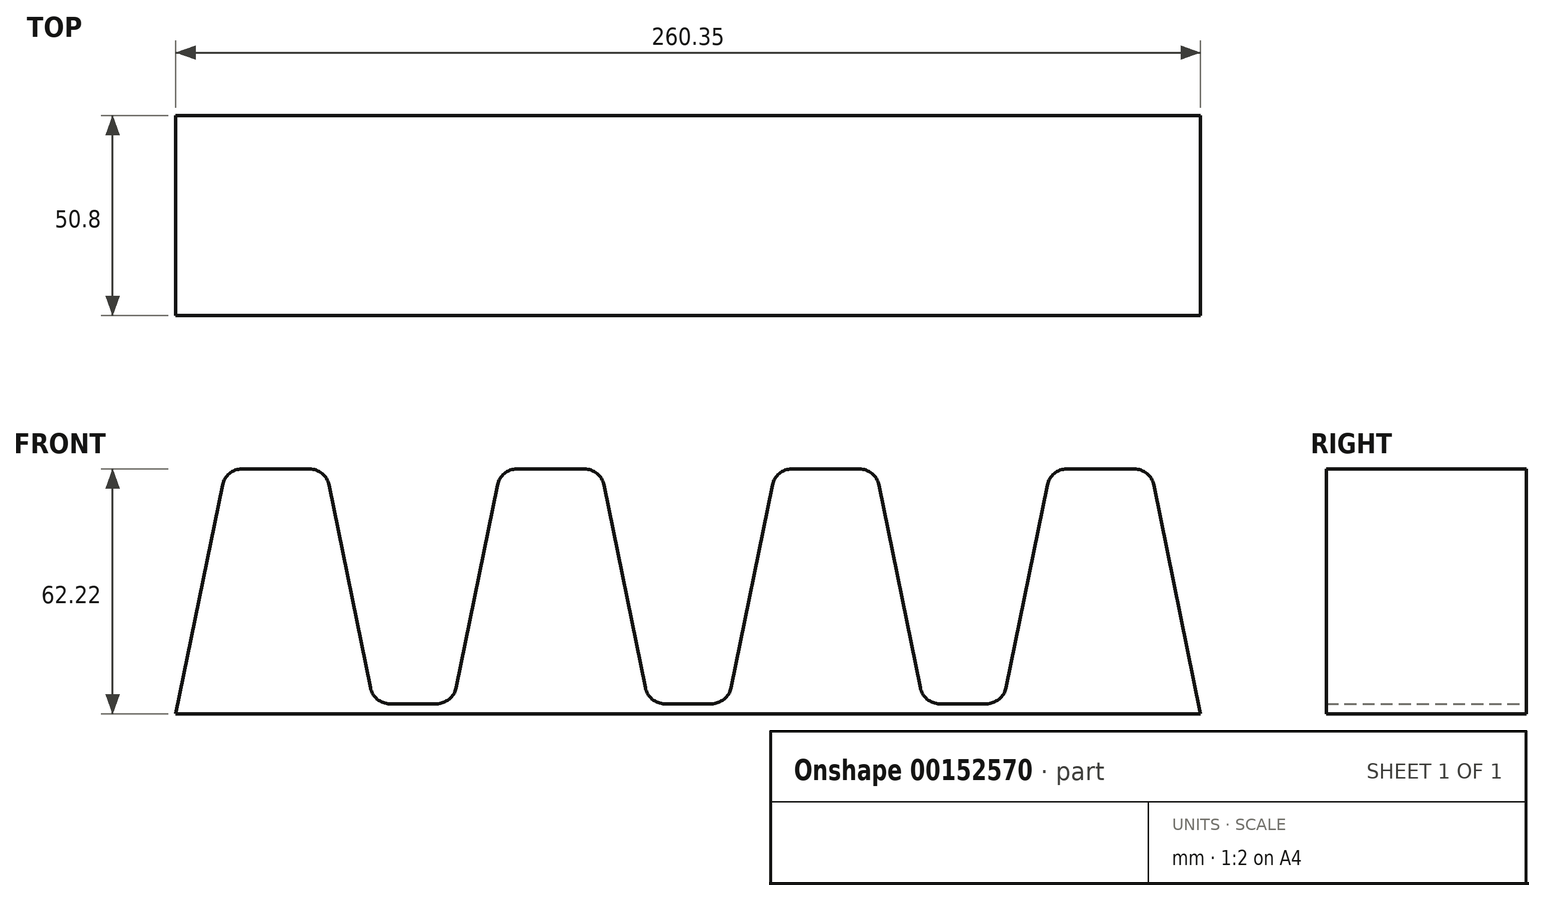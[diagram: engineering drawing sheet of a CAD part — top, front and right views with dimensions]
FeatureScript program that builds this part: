
annotation { "Feature Type Name" : "Feature", "Feature Type Description" : "" }
export const myFeature = defineFeature(function(context is Context, id is Id, definition is map)
    precondition{}
    {
        {
            var Q0;
            Q0=qCreatedBy(makeId("Front.planeOp"),FACE);
            var sketch = newSketch(context, id + "F0", { "sketchPlane" : qUnion([Q0])});
            skLineSegment(sketch, "E0", {"start": v(-120.65, -27.54) * mm, "end": v(-107.95, 34.68) * mm});
            skLineSegment(sketch, "E1", {"start": v(-107.95, 34.68) * mm, "end": v(-82.55, 34.68) * mm});
            skLineSegment(sketch, "E2", {"start": v(-82.55, 34.68) * mm, "end": v(-69.85, -27.54) * mm});
            skLineSegment(sketch, "E3", {"start": v(-69.85, -27.54) * mm, "end": v(-50.8, -27.54) * mm});
            skLineSegment(sketch, "E4", {"start": v(-50.8, -27.54) * mm, "end": v(-38.1, 34.68) * mm});
            skLineSegment(sketch, "E5", {"start": v(-38.1, 34.68) * mm, "end": v(-12.7, 34.68) * mm});
            skLineSegment(sketch, "E6", {"start": v(-12.7, 34.68) * mm, "end": v(0, -27.54) * mm});
            skLineSegment(sketch, "E7", {"start": v(0, -27.54) * mm, "end": v(19.05, -27.54) * mm});
            skLineSegment(sketch, "E8", {"start": v(19.05, -27.54) * mm, "end": v(31.75, 34.68) * mm});
            skLineSegment(sketch, "E9", {"start": v(31.75, 34.68) * mm, "end": v(57.15, 34.68) * mm});
            skLineSegment(sketch, "E10", {"start": v(57.15, 34.68) * mm, "end": v(69.85, -27.54) * mm});
            skLineSegment(sketch, "E11", {"start": v(69.85, -27.54) * mm, "end": v(88.9, -27.54) * mm});
            skLineSegment(sketch, "E12", {"start": v(88.9, -27.54) * mm, "end": v(101.6, 34.68) * mm});
            skLineSegment(sketch, "E13", {"start": v(-120.65, -27.54) * mm, "end": v(-69.85, -27.54) * mm});
            skLineSegment(sketch, "E14", {"start": v(-50.8, -27.54) * mm, "end": v(0, -27.54) * mm});
            skLineSegment(sketch, "E15", {"start": v(19.05, -27.54) * mm, "end": v(69.85, -27.54) * mm});
            skLineSegment(sketch, "E16", {"start": v(101.6, 34.68) * mm, "end": v(127, 34.68) * mm});
            skLineSegment(sketch, "E17", {"start": v(88.9, -27.54) * mm, "end": v(139.7, -27.54) * mm});
            skLineSegment(sketch, "E18", {"start": v(139.7, -27.54) * mm, "end": v(127, 34.68) * mm});
            skLineSegment(sketch, "E19", {"start": v(89.43, -24.96) * mm, "end": v(69.32, -24.96) * mm});
            skLineSegment(sketch, "E20", {"start": v(69.32, -24.96) * mm, "end": v(69.85, -27.54) * mm});
            skLineSegment(sketch, "E21", {"start": v(19.58, -24.96) * mm, "end": v(-0.53, -24.96) * mm});
            skLineSegment(sketch, "E22", {"start": v(-0.53, -24.96) * mm, "end": v(0, -27.54) * mm});
            skLineSegment(sketch, "E23", {"start": v(-50.27, -24.96) * mm, "end": v(-70.38, -24.96) * mm});
            skSolve(sketch);
        }
        {
            var Q0;
            Q0 = qSketchRegion(id + "F0", true);
            extrude(context, id + "F1", {"entities" : qUnion([Q0]), "depth" : 50.8 * mm});
        }
        {
            var Q0;
            Q0=makeQuery(id+"F1.opExtrude","SWEPT_EDGE",EDGE,{"disambiguationData":[OSD([sQuery(id+"F0.wireOp",EDGE,"E4"),sQuery(id+"F0.wireOp",EDGE,"E23")])]});
            fillet(context, id + "F2", {"entities" : qUnion([Q0]), "radius" : 5.08 * mm, "tangentPropagation" : true, "allowEdgeOverflow" : false});
        }
        {
            var Q0;
            Q0=makeQuery(id+"F1.opExtrude","SWEPT_EDGE",EDGE,{"disambiguationData":[OSD([sQuery(id+"F0.wireOp",EDGE,"E2"),sQuery(id+"F0.wireOp",EDGE,"E23")])]});
            fillet(context, id + "F3", {"entities" : qUnion([Q0]), "radius" : 5.08 * mm, "tangentPropagation" : true, "allowEdgeOverflow" : false});
        }
        {
            var Q0;
            Q0=makeQuery(id+"F1.opExtrude","SWEPT_EDGE",EDGE,{"disambiguationData":[OSD([sQuery(id+"F0.wireOp",EDGE,"E8"),sQuery(id+"F0.wireOp",EDGE,"E21")])]});
            fillet(context, id + "F4", {"entities" : qUnion([Q0]), "radius" : 5.08 * mm, "tangentPropagation" : true, "allowEdgeOverflow" : false});
        }
        {
            var Q0;
            Q0=makeQuery(id+"F1.opExtrude","SWEPT_EDGE",EDGE,{"disambiguationData":[OSD([sQuery(id+"F0.wireOp",EDGE,"E6"),sQuery(id+"F0.wireOp",EDGE,"E21"),sQuery(id+"F0.wireOp",EDGE,"E22")])]});
            fillet(context, id + "F5", {"entities" : qUnion([Q0]), "radius" : 5.08 * mm, "tangentPropagation" : true, "allowEdgeOverflow" : false});
        }
        {
            var Q0;
            Q0=makeQuery(id+"F1.opExtrude","SWEPT_EDGE",EDGE,{"disambiguationData":[OSD([sQuery(id+"F0.wireOp",EDGE,"E10"),sQuery(id+"F0.wireOp",EDGE,"E19"),sQuery(id+"F0.wireOp",EDGE,"E20")])]});
            fillet(context, id + "F6", {"entities" : qUnion([Q0]), "radius" : 5.08 * mm, "tangentPropagation" : true, "allowEdgeOverflow" : false});
        }
        {
            var Q0;
            Q0=makeQuery(id+"F1.opExtrude","SWEPT_EDGE",EDGE,{"disambiguationData":[OSD([sQuery(id+"F0.wireOp",EDGE,"E12"),sQuery(id+"F0.wireOp",EDGE,"E19")])]});
            fillet(context, id + "F7", {"entities" : qUnion([Q0]), "radius" : 5.08 * mm, "tangentPropagation" : true, "allowEdgeOverflow" : false});
        }
        {
            var Q0;
            Q0=makeQuery(id+"F1.opExtrude","SWEPT_EDGE",EDGE,{"disambiguationData":[OSD([sQuery(id+"F0.wireOp",EDGE,"E1"),sQuery(id+"F0.wireOp",EDGE,"E2")])]});
            fillet(context, id + "F8", {"entities" : qUnion([Q0]), "radius" : 5.08 * mm, "tangentPropagation" : true, "allowEdgeOverflow" : false});
        }
        {
            var Q0;
            Q0=makeQuery(id+"F1.opExtrude","SWEPT_EDGE",EDGE,{"disambiguationData":[OSD([sQuery(id+"F0.wireOp",EDGE,"E4"),sQuery(id+"F0.wireOp",EDGE,"E5")])]});
            fillet(context, id + "F9", {"entities" : qUnion([Q0]), "radius" : 5.08 * mm, "tangentPropagation" : true, "allowEdgeOverflow" : false});
        }
        {
            var Q0;
            Q0=makeQuery(id+"F1.opExtrude","SWEPT_EDGE",EDGE,{"disambiguationData":[OSD([sQuery(id+"F0.wireOp",EDGE,"E5"),sQuery(id+"F0.wireOp",EDGE,"E6")])]});
            fillet(context, id + "F10", {"entities" : qUnion([Q0]), "radius" : 5.08 * mm, "tangentPropagation" : true, "allowEdgeOverflow" : false});
        }
        {
            var Q0;
            Q0=makeQuery(id+"F1.opExtrude","SWEPT_EDGE",EDGE,{"disambiguationData":[OSD([sQuery(id+"F0.wireOp",EDGE,"E8"),sQuery(id+"F0.wireOp",EDGE,"E9")])]});
            fillet(context, id + "F11", {"entities" : qUnion([Q0]), "radius" : 5.08 * mm, "tangentPropagation" : true, "allowEdgeOverflow" : false});
        }
        {
            var Q0;
            Q0=makeQuery(id+"F1.opExtrude","SWEPT_EDGE",EDGE,{"disambiguationData":[OSD([sQuery(id+"F0.wireOp",EDGE,"E9"),sQuery(id+"F0.wireOp",EDGE,"E10")])]});
            fillet(context, id + "F12", {"entities" : qUnion([Q0]), "radius" : 5.08 * mm, "tangentPropagation" : true, "allowEdgeOverflow" : false});
        }
        {
            var Q0;
            Q0=makeQuery(id+"F1.opExtrude","SWEPT_EDGE",EDGE,{"disambiguationData":[OSD([sQuery(id+"F0.wireOp",EDGE,"E12"),sQuery(id+"F0.wireOp",EDGE,"E16")])]});
            fillet(context, id + "F13", {"entities" : qUnion([Q0]), "radius" : 5.08 * mm, "tangentPropagation" : true, "allowEdgeOverflow" : false});
        }
        {
            var Q0;
            Q0=makeQuery(id+"F1.opExtrude","SWEPT_EDGE",EDGE,{"disambiguationData":[OSD([sQuery(id+"F0.wireOp",EDGE,"E16"),sQuery(id+"F0.wireOp",EDGE,"E18")])]});
            fillet(context, id + "F14", {"entities" : qUnion([Q0]), "radius" : 5.08 * mm, "tangentPropagation" : true, "allowEdgeOverflow" : false});
        }
        {
            var Q0;
            Q0=makeQuery(id+"F1.opExtrude","SWEPT_EDGE",EDGE,{"disambiguationData":[OSD([sQuery(id+"F0.wireOp",EDGE,"E0"),sQuery(id+"F0.wireOp",EDGE,"E1")])]});
            fillet(context, id + "F15", {"entities" : qUnion([Q0]), "radius" : 5.08 * mm, "tangentPropagation" : true, "allowEdgeOverflow" : false});
        }
    });
